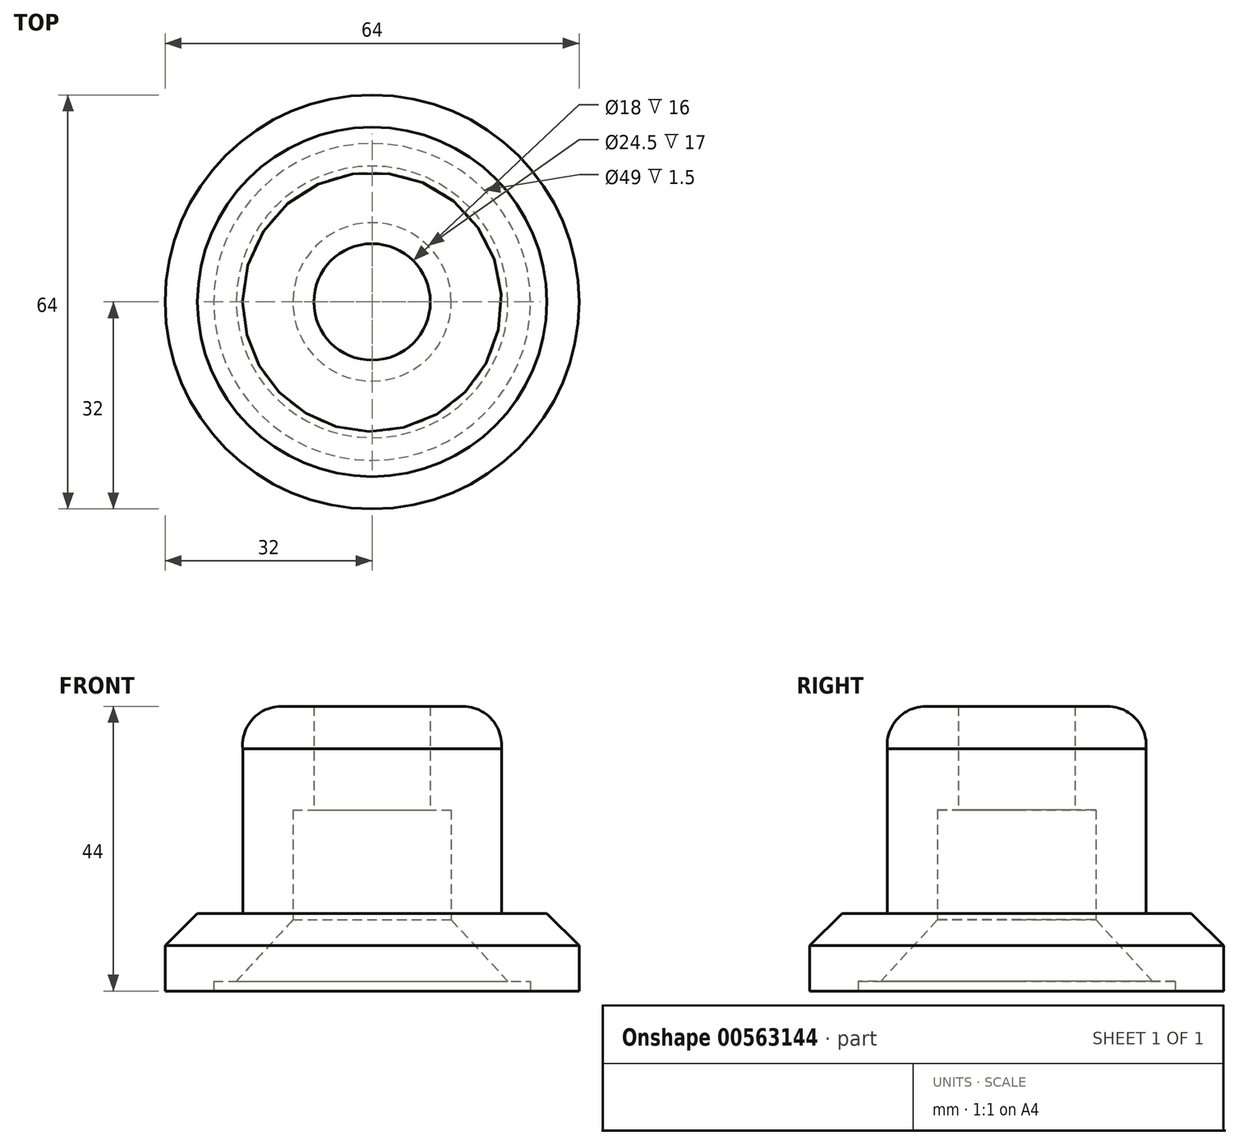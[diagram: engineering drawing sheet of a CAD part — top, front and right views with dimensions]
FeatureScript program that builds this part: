
annotation { "Feature Type Name" : "Feature", "Feature Type Description" : "" }
export const myFeature = defineFeature(function(context is Context, id is Id, definition is map)
    precondition{}
    {
        {
            var Q0;
            Q0=qCreatedBy(makeId("Front.planeOp"),FACE);
            var sketch = newSketch(context, id + "F0", { "sketchPlane" : qUnion([Q0])});
            skLineSegment(sketch, "E0", {"start": v(0, 0) * mm, "end": v(32, 0) * mm, "construction": true});
            skPoint(sketch, "E1", {"position": v(12.25, 0) * mm});
            skPoint(sketch, "E2.end.orphan", {"position": v(12.25, 2.28) * mm});
            skLineSegment(sketch, "E3", {"start": v(12.25, 0) * mm, "end": v(12.25, 43.88) * mm, "construction": true});
            skPoint(sketch, "E4", {"position": v(24.5, 0) * mm});
            skPoint(sketch, "E5", {"position": v(32, 1.5) * mm});
            skLineSegment(sketch, "E6", {"start": v(32, 0) * mm, "end": v(32, 11) * mm});
            skPoint(sketch, "E7", {"position": v(32, 7) * mm});
            skPoint(sketch, "E8", {"position": v(21, 0) * mm});
            skPoint(sketch, "E9", {"position": v(24.5, 1.5) * mm});
            skLineSegment(sketch, "E10", {"start": v(32, 0) * mm, "end": v(24.5, 0) * mm});
            skLineSegment(sketch, "E11", {"start": v(24.5, 1.5) * mm, "end": v(24.5, 0) * mm});
            skLineSegment(sketch, "E12", {"start": v(21, 0) * mm, "end": v(21, 2.7) * mm, "construction": true});
            skLineSegment(sketch, "E13", {"start": v(24.5, 1.5) * mm, "end": v(21, 1.5) * mm});
            skLineSegment(sketch, "E14", {"start": v(32, 11) * mm, "end": v(4.88, 11) * mm, "construction": true});
            skPoint(sketch, "E15", {"position": v(12.25, 11) * mm});
            skLineSegment(sketch, "E16", {"start": v(32, 11) * mm, "end": v(32, 12) * mm});
            skPoint(sketch, "E17", {"position": v(32, 12) * mm});
            skPoint(sketch, "E18.orphan", {"position": v(32, 13) * mm});
            skLineSegment(sketch, "E19", {"start": v(21, 2.7) * mm, "end": v(21, 11) * mm, "construction": true});
            skLineSegment(sketch, "E20", {"start": v(32, 12) * mm, "end": v(27, 12) * mm, "construction": true});
            skLineSegment(sketch, "E21", {"start": v(12.25, 11) * mm, "end": v(12.25, 28) * mm});
            skLineSegment(sketch, "E22", {"start": v(21, 1.5) * mm, "end": v(12.25, 11) * mm});
            skLineSegment(sketch, "E23", {"start": v(32, 7) * mm, "end": v(27, 12) * mm});
            skPoint(sketch, "E24", {"position": v(8.36, 27.68) * mm});
            skLineSegment(sketch, "E25", {"start": v(12.25, 28) * mm, "end": v(9, 28) * mm});
            skLineSegment(sketch, "E26", {"start": v(9, 28) * mm, "end": v(9, 44) * mm});
            skLineSegment(sketch, "E27", {"start": v(14.05, 44) * mm, "end": v(9, 44) * mm});
            skPoint(sketch, "E28.end.orphan", {"position": v(21, 28) * mm});
            skLineSegment(sketch, "E29", {"start": v(27, 12) * mm, "end": v(20, 12) * mm});
            skLineSegment(sketch, "E30", {"start": v(20, 38.54) * mm, "end": v(20, 12) * mm});
            skLineSegment(sketch, "E31", {"start": v(21, 28) * mm, "end": v(18.76, 28) * mm, "construction": true});
            skPoint(sketch, "E31.endSnap0", {"position": v(20, 28) * mm});
            skPoint(sketch, "E32", {"position": v(20, 37.46) * mm});
            skPoint(sketch, "E33", {"position": v(14, 44) * mm});
            skLineSegment(sketch, "E34", {"start": v(14, 44) * mm, "end": v(14, 37.88) * mm, "construction": true});
            skLineSegment(sketch, "E35", {"start": v(20, 37.46) * mm, "end": v(2.86, 37.46) * mm, "construction": true});
            skPoint(sketch, "E36", {"position": v(14, 37.46) * mm});
            skArc(sketch, "E37", {"start": v(20, 37.46) * mm, "mid": v(18.45, 42.06) * mm, "end": v(14, 44) * mm});
            skPoint(sketch, "E38.orphan", {"position": v(20, 44) * mm});
            skLineSegment(sketch, "E39", {"start": v(0, 0) * mm, "end": v(0, 47.07) * mm, "construction": true});
            skSolve(sketch);
        }
        {
            var Q0;
            Q0 = qSketchRegion(id + "F0", true);
            var Q1;
            Q1=sQuery(id+"F0.wireOp",EDGE,"E39");
            revolve(context, id + "F1", {"entities" : qUnion([Q0]), "axis" : qUnion([Q1]), "revolveType" : RevolveType.FULL});
        }
    });
